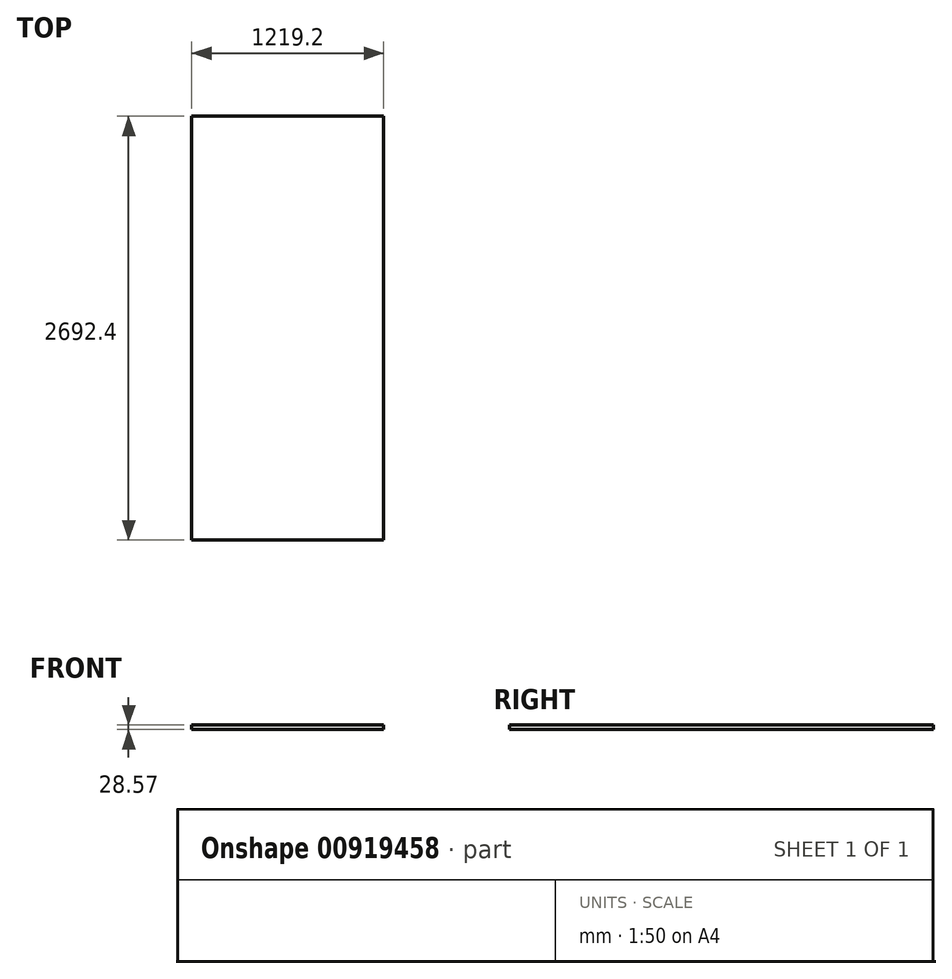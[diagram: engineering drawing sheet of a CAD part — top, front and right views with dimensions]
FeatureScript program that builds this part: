
annotation { "Feature Type Name" : "Feature", "Feature Type Description" : "" }
export const myFeature = defineFeature(function(context is Context, id is Id, definition is map)
    precondition{}
    {
        {
            var Q0;
            Q0=qCreatedBy(makeId("Top.planeOp"),FACE);
            var sketch = newSketch(context, id + "F0", { "sketchPlane" : qUnion([Q0])});
            skLineSegment(sketch, "E0.bottom", {"start": v(609.6, 1346.2) * mm, "end": v(-609.6, 1346.2) * mm});
            skLineSegment(sketch, "E0.top", {"start": v(609.6, -1346.2) * mm, "end": v(-609.6, -1346.2) * mm});
            skLineSegment(sketch, "E0.left", {"start": v(609.6, 1346.2) * mm, "end": v(609.6, -1346.2) * mm});
            skLineSegment(sketch, "E0.right", {"start": v(-609.6, 1346.2) * mm, "end": v(-609.6, -1346.2) * mm});
            skPoint(sketch, "E0.middle", {"position": v(0, 0) * mm});
            skSolve(sketch);
        }
        {
            var Q0;
            Q0=makeQuery(id+"F0.imprint","IMPRINT",FACE,{"disambiguationData":[TD([[makeQuery(id+"F0.imprint","IMPRINT",EDGE,{"derivedFrom":sQuery(id+"F0.wireOp",EDGE,"E0.bottom")}),1.0]])]});
            extrude(context, id + "F1", {"entities" : qUnion([Q0]), "depth" : 28.57 * mm, "offsetDistance" : 25.4 * mm});
        }
    });
